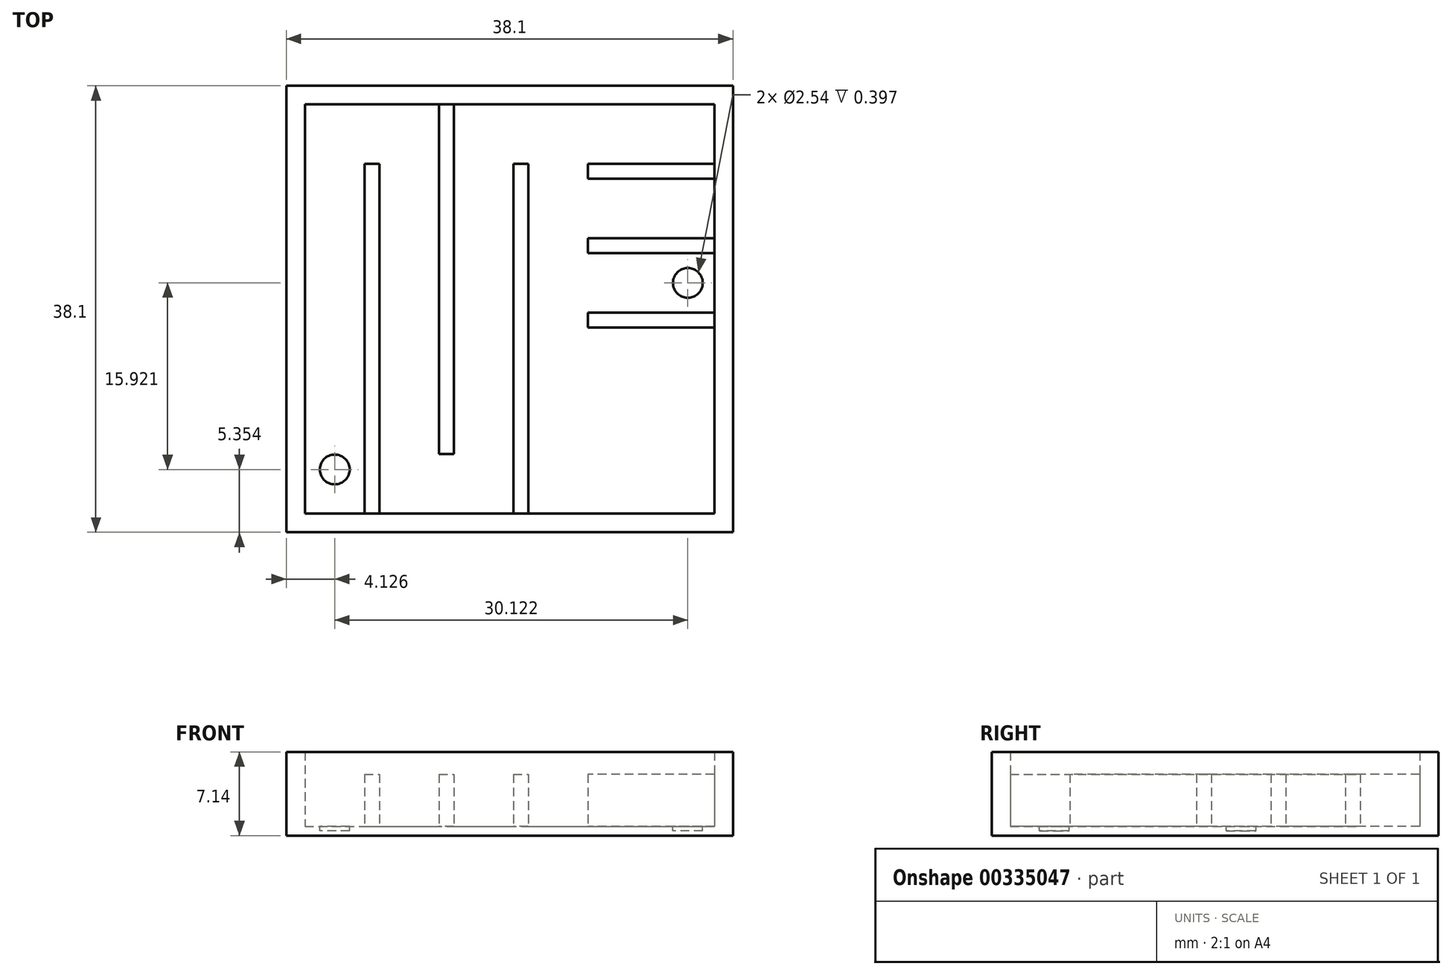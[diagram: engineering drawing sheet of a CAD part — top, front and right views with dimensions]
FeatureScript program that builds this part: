
annotation { "Feature Type Name" : "Feature", "Feature Type Description" : "" }
export const myFeature = defineFeature(function(context is Context, id is Id, definition is map)
    precondition{}
    {
        {
            var Q0;
            Q0=qCreatedBy(makeId("Top.planeOp"),FACE);
            var sketch = newSketch(context, id + "F0", { "sketchPlane" : qUnion([Q0])});
            skLineSegment(sketch, "E0.bottom", {"start": v(-18.83, 25.93) * mm, "end": v(19.27, 25.93) * mm});
            skLineSegment(sketch, "E0.top", {"start": v(-18.83, -12.17) * mm, "end": v(19.27, -12.17) * mm});
            skLineSegment(sketch, "E0.left", {"start": v(-18.83, 25.93) * mm, "end": v(-18.83, -12.17) * mm});
            skLineSegment(sketch, "E0.right", {"start": v(19.27, 25.93) * mm, "end": v(19.27, -12.17) * mm});
            skSolve(sketch);
        }
        {
            var Q0;
            Q0=makeQuery(id+"F0.imprint","IMPRINT",FACE,{"disambiguationData":[TD([[makeQuery(id+"F0.imprint","IMPRINT",EDGE,{"derivedFrom":sQuery(id+"F0.wireOp",EDGE,"E0.bottom")}),-1.0]])]});
            extrude(context, id + "F1", {"entities" : qUnion([Q0]), "depth" : 0.8 * mm});
        }
        {
            var Q0;
            Q0=makeQuery(id+"F1.opExtrude","CAP_FACE",FACE,{"disambiguationData":[OSD([sQuery(id+"F0.wireOp",EDGE,"E0.bottom"),sQuery(id+"F0.wireOp",EDGE,"E0.top"),sQuery(id+"F0.wireOp",EDGE,"E0.left"),sQuery(id+"F0.wireOp",EDGE,"E0.right")])],"isStart":false});
            var sketch = newSketch(context, id + "F2", { "sketchPlane" : qUnion([Q0])});
            skLineSegment(sketch, "E1.0", {"start": v(-17.24, 24.34) * mm, "end": v(17.68, 24.34) * mm});
            skLineSegment(sketch, "E1.1", {"start": v(-17.24, 24.34) * mm, "end": v(-17.24, -10.58) * mm});
            skLineSegment(sketch, "E1.2", {"start": v(-17.24, -10.58) * mm, "end": v(17.68, -10.58) * mm});
            skLineSegment(sketch, "E1.3", {"start": v(17.68, 24.34) * mm, "end": v(17.68, -10.58) * mm});
            skSolve(sketch);
        }
        {
            var Q0;
            Q0=makeQuery(id+"F2.imprint","IMPRINT",FACE,{"disambiguationData":[TD([[makeQuery(id+"F2.imprint","IMPRINT",EDGE,{"derivedFrom":sQuery(id+"F2.wireOp",EDGE,"E1.0")}),1.0]])]});
            extrude(context, id + "F3", {"entities" : qUnion([Q0]), "operationType" : NewBodyOperationType.ADD, "depth" : 6.35 * mm});
        }
        {
            var Q0;
            Q0=makeQuery(id+"F1.opExtrude","CAP_FACE",FACE,{"disambiguationData":[OSD([sQuery(id+"F0.wireOp",EDGE,"E0.bottom"),sQuery(id+"F0.wireOp",EDGE,"E0.top"),sQuery(id+"F0.wireOp",EDGE,"E0.left"),sQuery(id+"F0.wireOp",EDGE,"E0.right")])],"isStart":false});
            var sketch = newSketch(context, id + "F4", { "sketchPlane" : qUnion([Q0])});
            skLineSegment(sketch, "E2.bottom", {"start": v(-12.16, -10.58) * mm, "end": v(-10.9, -10.58) * mm});
            skLineSegment(sketch, "E2.top", {"start": v(-12.16, 19.26) * mm, "end": v(-10.9, 19.26) * mm});
            skLineSegment(sketch, "E2.left", {"start": v(-12.16, -10.58) * mm, "end": v(-12.16, 19.26) * mm});
            skLineSegment(sketch, "E2.right", {"start": v(-10.9, -10.58) * mm, "end": v(-10.9, 19.26) * mm});
            skLineSegment(sketch, "E3.bottom", {"start": v(-4.54, 24.34) * mm, "end": v(-5.81, 24.34) * mm});
            skLineSegment(sketch, "E3.top", {"start": v(-4.54, -5.5) * mm, "end": v(-5.81, -5.5) * mm});
            skLineSegment(sketch, "E3.left", {"start": v(-4.54, 24.34) * mm, "end": v(-4.54, -5.5) * mm});
            skLineSegment(sketch, "E3.right", {"start": v(-5.81, 24.34) * mm, "end": v(-5.81, -5.5) * mm});
            skLineSegment(sketch, "E4.bottom", {"start": v(1.8, -10.58) * mm, "end": v(0.54, -10.58) * mm});
            skLineSegment(sketch, "E4.top", {"start": v(1.8, 19.26) * mm, "end": v(0.54, 19.26) * mm});
            skLineSegment(sketch, "E4.left", {"start": v(1.8, -10.58) * mm, "end": v(1.8, 19.26) * mm});
            skLineSegment(sketch, "E4.right", {"start": v(0.54, -10.58) * mm, "end": v(0.54, 19.26) * mm});
            skLineSegment(sketch, "E5.bottom", {"start": v(17.68, 19.26) * mm, "end": v(6.89, 19.26) * mm});
            skLineSegment(sketch, "E5.top", {"start": v(17.68, 18) * mm, "end": v(6.89, 18) * mm});
            skLineSegment(sketch, "E5.left", {"start": v(17.68, 19.26) * mm, "end": v(17.68, 18) * mm});
            skLineSegment(sketch, "E5.right", {"start": v(6.89, 19.26) * mm, "end": v(6.89, 18) * mm});
            skLineSegment(sketch, "E6.bottom", {"start": v(17.68, 12.91) * mm, "end": v(6.89, 12.91) * mm});
            skLineSegment(sketch, "E6.top", {"start": v(17.68, 11.64) * mm, "end": v(6.89, 11.64) * mm});
            skLineSegment(sketch, "E6.left", {"start": v(17.68, 12.91) * mm, "end": v(17.68, 11.64) * mm});
            skLineSegment(sketch, "E6.right", {"start": v(6.89, 12.91) * mm, "end": v(6.89, 11.64) * mm});
            skSolve(sketch);
        }
        {
            var Q0;
            Q0=makeQuery(id+"F4.imprint","IMPRINT",FACE,{"disambiguationData":[TD([[makeQuery(id+"F4.imprint","IMPRINT",EDGE,{"derivedFrom":sQuery(id+"F4.wireOp",EDGE,"E2.bottom")}),1.0]])]});
            var Q1;
            Q1=makeQuery(id+"F4.imprint","IMPRINT",FACE,{"disambiguationData":[TD([[makeQuery(id+"F4.imprint","IMPRINT",EDGE,{"derivedFrom":sQuery(id+"F4.wireOp",EDGE,"E3.bottom")}),-1.0]])]});
            var Q2;
            Q2=makeQuery(id+"F4.imprint","IMPRINT",FACE,{"disambiguationData":[TD([[makeQuery(id+"F4.imprint","IMPRINT",EDGE,{"derivedFrom":sQuery(id+"F4.wireOp",EDGE,"E4.bottom")}),1.0]])]});
            var Q3;
            Q3=makeQuery(id+"F4.imprint","IMPRINT",FACE,{"disambiguationData":[TD([[makeQuery(id+"F4.imprint","IMPRINT",EDGE,{"derivedFrom":sQuery(id+"F4.wireOp",EDGE,"E6.bottom")}),1.0]])]});
            var Q4;
            Q4=makeQuery(id+"F4.imprint","IMPRINT",FACE,{"disambiguationData":[TD([[makeQuery(id+"F4.imprint","IMPRINT",EDGE,{"derivedFrom":sQuery(id+"F4.wireOp",EDGE,"E5.bottom")}),1.0]])]});
            extrude(context, id + "F5", {"entities" : qUnion([Q0, Q1, Q2, Q3, Q4]), "operationType" : NewBodyOperationType.ADD, "depth" : 4.44 * mm});
        }
        {
            var Q0;
            Q0=makeQuery(id+"F1.opExtrude","CAP_FACE",FACE,{"disambiguationData":[OSD([sQuery(id+"F0.wireOp",EDGE,"E0.bottom"),sQuery(id+"F0.wireOp",EDGE,"E0.top"),sQuery(id+"F0.wireOp",EDGE,"E0.left"),sQuery(id+"F0.wireOp",EDGE,"E0.right")])],"isStart":false});
            var sketch = newSketch(context, id + "F6", { "sketchPlane" : qUnion([Q0])});
            skLineSegment(sketch, "E7.bottom", {"start": v(17.68, 6.56) * mm, "end": v(6.89, 6.56) * mm});
            skLineSegment(sketch, "E7.top", {"start": v(17.68, 5.3) * mm, "end": v(6.89, 5.3) * mm});
            skLineSegment(sketch, "E7.left", {"start": v(17.68, 6.56) * mm, "end": v(17.68, 5.3) * mm});
            skLineSegment(sketch, "E7.right", {"start": v(6.89, 6.56) * mm, "end": v(6.89, 5.3) * mm});
            skSolve(sketch);
        }
        {
            var Q0;
            Q0=makeQuery(id+"F6.imprint","IMPRINT",FACE,{"disambiguationData":[TD([[makeQuery(id+"F6.imprint","IMPRINT",EDGE,{"derivedFrom":sQuery(id+"F6.wireOp",EDGE,"E7.bottom")}),1.0]])]});
            extrude(context, id + "F7", {"entities" : qUnion([Q0]), "operationType" : NewBodyOperationType.ADD, "depth" : 4.44 * mm});
        }
        {
            var Q0;
            Q0=makeQuery(id+"F1.opExtrude","CAP_FACE",FACE,{"disambiguationData":[OSD([sQuery(id+"F0.wireOp",EDGE,"E0.bottom"),sQuery(id+"F0.wireOp",EDGE,"E0.top"),sQuery(id+"F0.wireOp",EDGE,"E0.left"),sQuery(id+"F0.wireOp",EDGE,"E0.right")])],"isStart":false});
            var sketch = newSketch(context, id + "F8", { "sketchPlane" : qUnion([Q0])});
            skLineSegment(sketch, "E8", {"start": v(-17.24, -10.58) * mm, "end": v(-12.16, -10.58) * mm});
            skCircle(sketch, "E9", {"center": v(-14.7, -6.82) * mm, "radius": 1.27 * mm});
            skPoint(sketch, "E9.centerSnap0", {"position": v(-14.7, -10.58) * mm});
            skSolve(sketch);
        }
        {
            var Q0;
            Q0=makeQuery(id+"F8.imprint","IMPRINT",FACE,{"disambiguationData":[TD([[makeQuery(id+"F8.imprint","IMPRINT",EDGE,{"derivedFrom":sQuery(id+"F8.wireOp",EDGE,"E9")}),1.0]])]});
            extrude(context, id + "F9", {"entities" : qUnion([Q0]), "operationType" : NewBodyOperationType.REMOVE, "depth" : 0.4 * mm});
        }
        {
            var Q0;
            Q0=makeQuery(id+"F1.opExtrude","CAP_FACE",FACE,{"disambiguationData":[OSD([sQuery(id+"F0.wireOp",EDGE,"E0.bottom"),sQuery(id+"F0.wireOp",EDGE,"E0.top"),sQuery(id+"F0.wireOp",EDGE,"E0.left"),sQuery(id+"F0.wireOp",EDGE,"E0.right")])],"isStart":false});
            var sketch = newSketch(context, id + "F10", { "sketchPlane" : qUnion([Q0])});
            skLineSegment(sketch, "E10", {"start": v(17.68, 11.64) * mm, "end": v(17.68, 6.56) * mm});
            skCircle(sketch, "E11", {"center": v(15.42, 9.1) * mm, "radius": 1.27 * mm});
            skPoint(sketch, "E11.centerSnap0", {"position": v(17.68, 9.1) * mm});
            skSolve(sketch);
        }
        {
            var Q0;
            Q0=makeQuery(id+"F10.imprint","IMPRINT",FACE,{"disambiguationData":[TD([[makeQuery(id+"F10.imprint","IMPRINT",EDGE,{"derivedFrom":sQuery(id+"F10.wireOp",EDGE,"E11")}),1.0]])]});
            extrude(context, id + "F11", {"entities" : qUnion([Q0]), "operationType" : NewBodyOperationType.REMOVE, "oppositeDirection" : true, "depth" : 0.4 * mm});
        }
        {
            var Q0;
            Q0=makeQuery(id+"F8.imprint","IMPRINT",FACE,{"disambiguationData":[TD([[makeQuery(id+"F8.imprint","IMPRINT",EDGE,{"derivedFrom":sQuery(id+"F8.wireOp",EDGE,"E9")}),1.0]])]});
            extrude(context, id + "F12", {"entities" : qUnion([Q0]), "operationType" : NewBodyOperationType.REMOVE, "oppositeDirection" : true, "depth" : 0.4 * mm});
        }
    });
